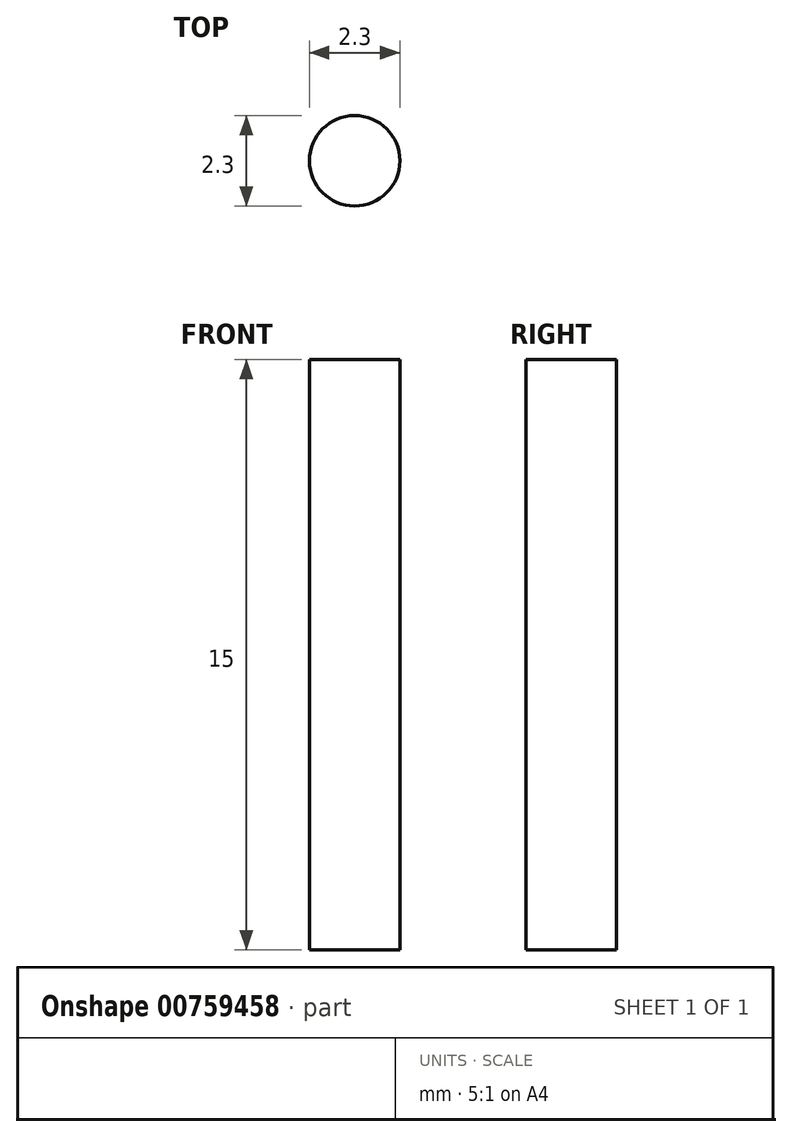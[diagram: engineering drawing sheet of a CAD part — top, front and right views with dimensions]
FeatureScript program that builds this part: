
annotation { "Feature Type Name" : "Feature", "Feature Type Description" : "" }
export const myFeature = defineFeature(function(context is Context, id is Id, definition is map)
    precondition{}
    {
        {
            var Q0;
            Q0=qCreatedBy(makeId("Top.planeOp"),FACE);
            var sketch = newSketch(context, id + "F0", { "sketchPlane" : qUnion([Q0])});
            skCircle(sketch, "E0", {"center": v(0, 0) * mm, "radius": 1.15 * mm});
            skSolve(sketch);
        }
        {
            var Q0;
            Q0=makeQuery(id+"F0.imprint","IMPRINT",FACE,{"disambiguationData":[TD([[makeQuery(id+"F0.imprint","IMPRINT",EDGE,{"derivedFrom":sQuery(id+"F0.wireOp",EDGE,"E0")}),1.0]])]});
            extrude(context, id + "F1", {"entities" : qUnion([Q0]), "oppositeDirection" : true, "depth" : 15 * mm, "offsetDistance" : 25 * mm});
        }
    });
